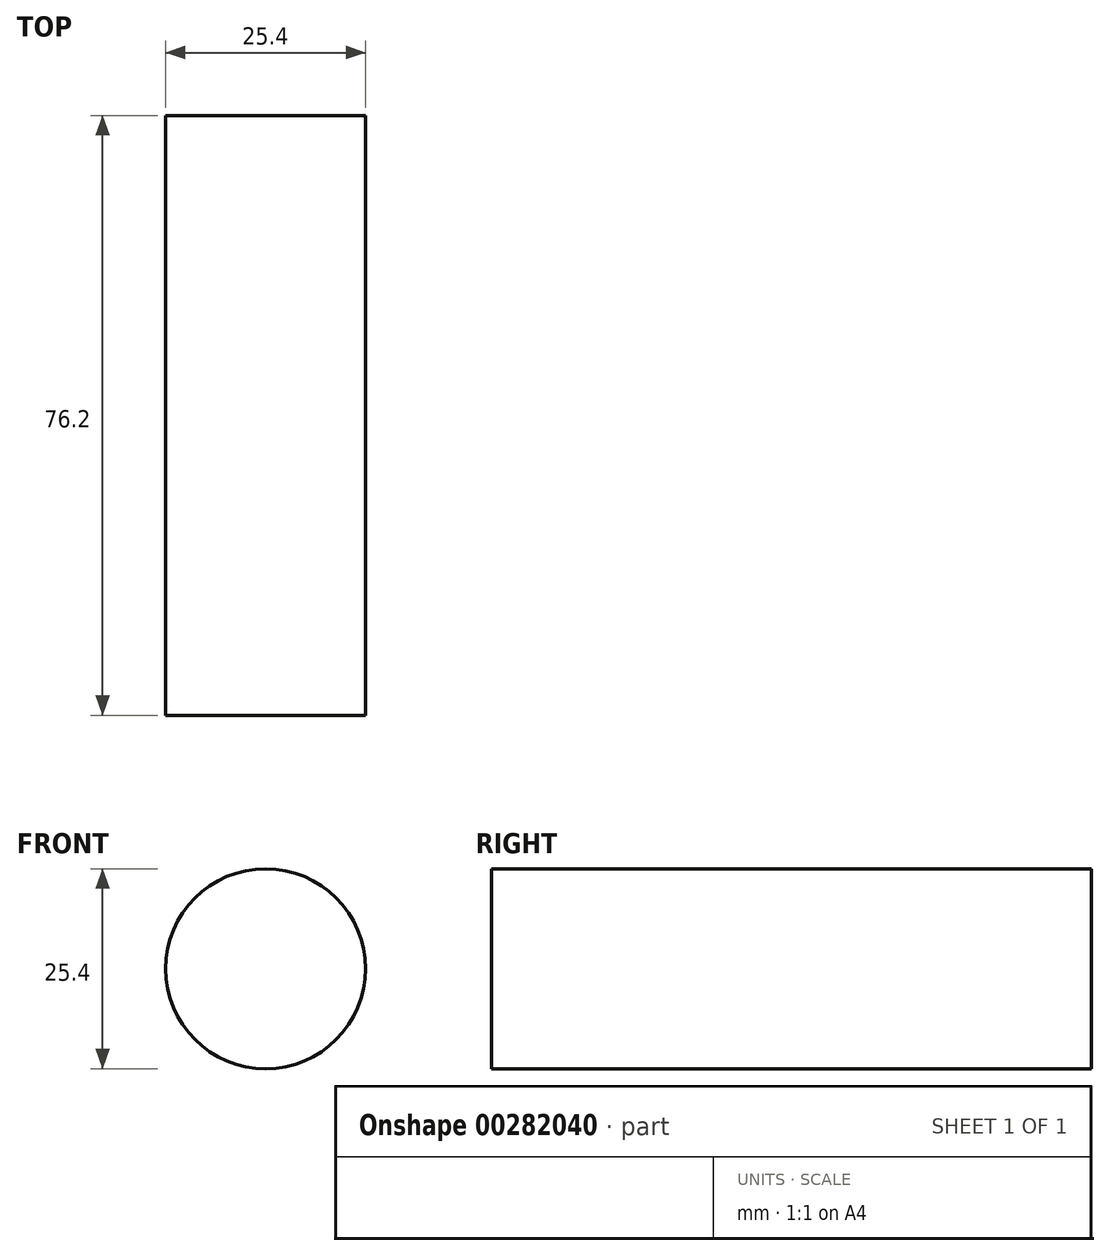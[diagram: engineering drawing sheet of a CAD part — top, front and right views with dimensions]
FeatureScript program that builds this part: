
annotation { "Feature Type Name" : "Feature", "Feature Type Description" : "" }
export const myFeature = defineFeature(function(context is Context, id is Id, definition is map)
    precondition{}
    {
        {
            var Q0;
            Q0=qCreatedBy(makeId("Front.planeOp"),FACE);
            var sketch = newSketch(context, id + "F0", { "sketchPlane" : qUnion([Q0])});
            skCircle(sketch, "E0", {"center": v(-31.87, 37.79) * mm, "radius": 12.7 * mm});
            skSolve(sketch);
        }
        {
            var Q0;
            Q0=makeQuery(id+"F0.imprint","IMPRINT",FACE,{"disambiguationData":[TD([[makeQuery(id+"F0.imprint","IMPRINT",EDGE,{"derivedFrom":sQuery(id+"F0.wireOp",EDGE,"E0")}),1.0]])]});
            extrude(context, id + "F1", {"entities" : qUnion([Q0]), "depth" : 76.2 * mm});
        }
    });
